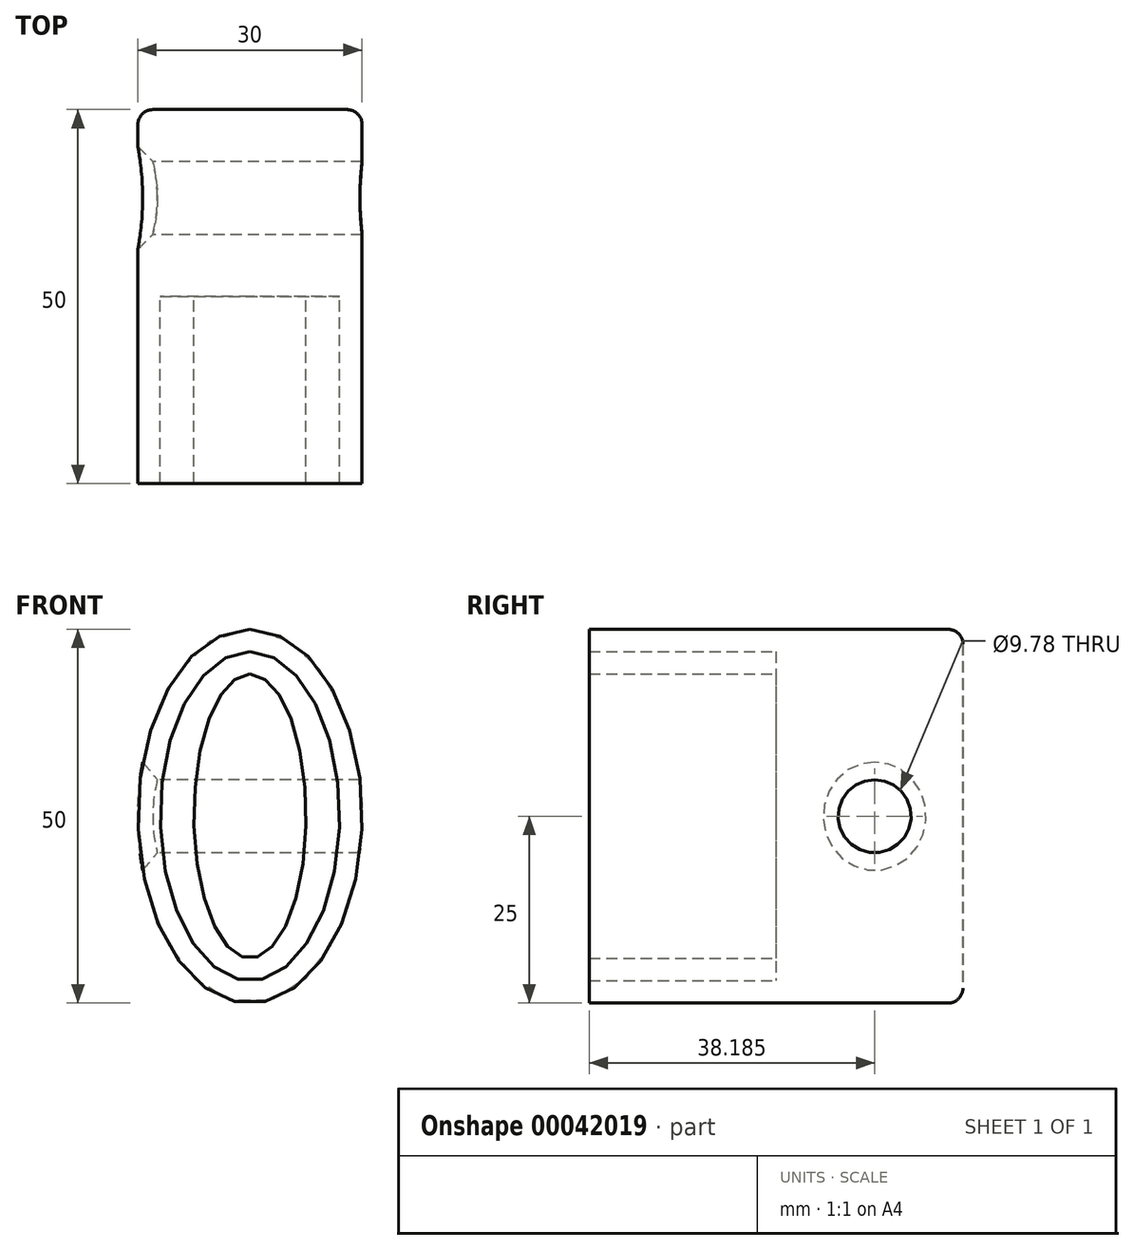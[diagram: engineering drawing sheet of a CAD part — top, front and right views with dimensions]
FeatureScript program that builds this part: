
annotation { "Feature Type Name" : "Feature", "Feature Type Description" : "" }
export const myFeature = defineFeature(function(context is Context, id is Id, definition is map)
    precondition{}
    {
        {
            var Q0;
            Q0=qCreatedBy(makeId("Front.planeOp"),FACE);
            var sketch = newSketch(context, id + "F0", { "sketchPlane" : qUnion([Q0])});
            skEllipse(sketch, "E0", {"center": v(0, 0) * mm, "majorRadius": 25 * mm, "minorRadius": 15 * mm, "majorAxis": v(0, 1)});
            skEllipse(sketch, "E1", {"center": v(0, 0) * mm, "majorRadius": 22 * mm, "minorRadius": 12 * mm, "majorAxis": v(0, 1)});
            skEllipse(sketch, "E2", {"center": v(0, 0) * mm, "majorRadius": 19 * mm, "minorRadius": 7.5 * mm, "majorAxis": v(0, 1)});
            skSolve(sketch);
        }
        {
            var Q0;
            Q0 = qSketchRegion(id + "F0", true);
            var Q1;
            Q1=makeQuery(id+"F0.imprint","IMPRINT",FACE,{"disambiguationData":[TD([[makeQuery(id+"F0.imprint","IMPRINT",EDGE,{"derivedFrom":sQuery(id+"F0.wireOp",EDGE,"E2")}),1.0]])]});
            extrude(context, id + "F1", {"entities" : qUnion([Q0, Q1]), "depth" : 25 * mm});
        }
        {
            var Q0;
            Q0=qCreatedBy(makeId("Front.planeOp"),FACE);
            var sketch = newSketch(context, id + "F2", { "sketchPlane" : qUnion([Q0])});
            skEllipse(sketch, "E3", {"center": v(0, 0) * mm, "majorRadius": 25 * mm, "minorRadius": 15 * mm, "majorAxis": v(0, 1)});
            skSolve(sketch);
        }
        {
            var Q0;
            Q0 = qSketchRegion(id + "F2", true);
            extrude(context, id + "F3", {"entities" : qUnion([Q0]), "oppositeDirection" : true, "depth" : 25 * mm});
        }
        {
            var Q0;
            Q0=makeQuery(id+"F1.opExtrude","SWEPT_BODY",BODY,{"disambiguationData":[OSD([sQuery(id+"F0.wireOp",EDGE,"E0"),sQuery(id+"F0.wireOp",EDGE,"E1")])]});
            var Q1;
            Q1=makeQuery(id+"F3.opExtrude","SWEPT_BODY",BODY,{"disambiguationData":[OSD([sQuery(id+"F2.wireOp",EDGE,"E3")])]});
            booleanBodies(context, id + "F4", {"operationType" : BooleanOperationType.UNION, "tools" : qUnion([Q0, Q1])});
        }
        {
            var Q0;
            Q0=qCreatedBy(makeId("Right.planeOp"),FACE);
            var sketch = newSketch(context, id + "F5", { "sketchPlane" : qUnion([Q0])});
            skCircle(sketch, "E4", {"center": v(13.18, 0) * mm, "radius": 4.9 * mm});
            skSolve(sketch);
        }
        {
            var Q0;
            Q0 = qSketchRegion(id + "F5", true);
            extrude(context, id + "F6", {"entities" : qUnion([Q0]), "depth" : 41 * mm});
        }
        {
            var Q0;
            Q0=makeQuery(id+"F6.opExtrude","SWEPT_BODY",BODY,{"disambiguationData":[OSD([sQuery(id+"F5.wireOp",EDGE,"E4")])]});
            transform(context, id + "F7", {"entities" : qUnion([Q0]), "transformType" : TransformType.TRANSLATION_3D, "dx" : -19.99 * mm, "dy" : 0 * mm, "dz" : 0 * mm, "makeCopy" : false});
        }
        {
            var Q0;
            Q0=makeQuery(id+"F6.opExtrude","SWEPT_BODY",BODY,{"disambiguationData":[OSD([sQuery(id+"F5.wireOp",EDGE,"E4")])]});
            var Q1;
            Q1=makeQuery(id+"F1.opExtrude","SWEPT_BODY",BODY,{"disambiguationData":[OSD([sQuery(id+"F0.wireOp",EDGE,"E0"),sQuery(id+"F0.wireOp",EDGE,"E1")])]});
            booleanBodies(context, id + "F8", {"operationType" : BooleanOperationType.SUBTRACTION, "tools" : qUnion([Q0]), "targets" : qUnion([Q1])});
        }
        {
            var Q0;
            Q0=makeQuery(id+"F8.opBoolean","INTERSECT",EDGE,{"disambiguationData":[OD(0.0)],"derivedFrom":[makeQuery(id+"F4.opBoolean","MERGE",FACE,{"derivedFrom":[makeQuery(id+"F1.opExtrude","SWEPT_FACE",FACE,{"disambiguationData":[OSD([sQuery(id+"F0.wireOp",EDGE,"E0")])]}),makeQuery(id+"F3.opExtrude","SWEPT_FACE",FACE,{"disambiguationData":[OSD([sQuery(id+"F2.wireOp",EDGE,"E3")])]})]}),makeQuery(id+"F6.opExtrude","SWEPT_FACE",FACE,{"disambiguationData":[OSD([sQuery(id+"F5.wireOp",EDGE,"E4")])]})]});
            chamfer(context, id + "F9", {"entities" : qUnion([Q0]), "width" : 2 * mm});
        }
        {
            var Q0;
            Q0=makeQuery(id+"F3.opExtrude","CAP_EDGE",EDGE,{"disambiguationData":[OSD([sQuery(id+"F2.wireOp",EDGE,"E3")])],"isStart":false});
            fillet(context, id + "F10", {"entities" : qUnion([Q0]), "radius" : 2 * mm, "tangentPropagation" : true, "allowEdgeOverflow" : false});
        }
    });
